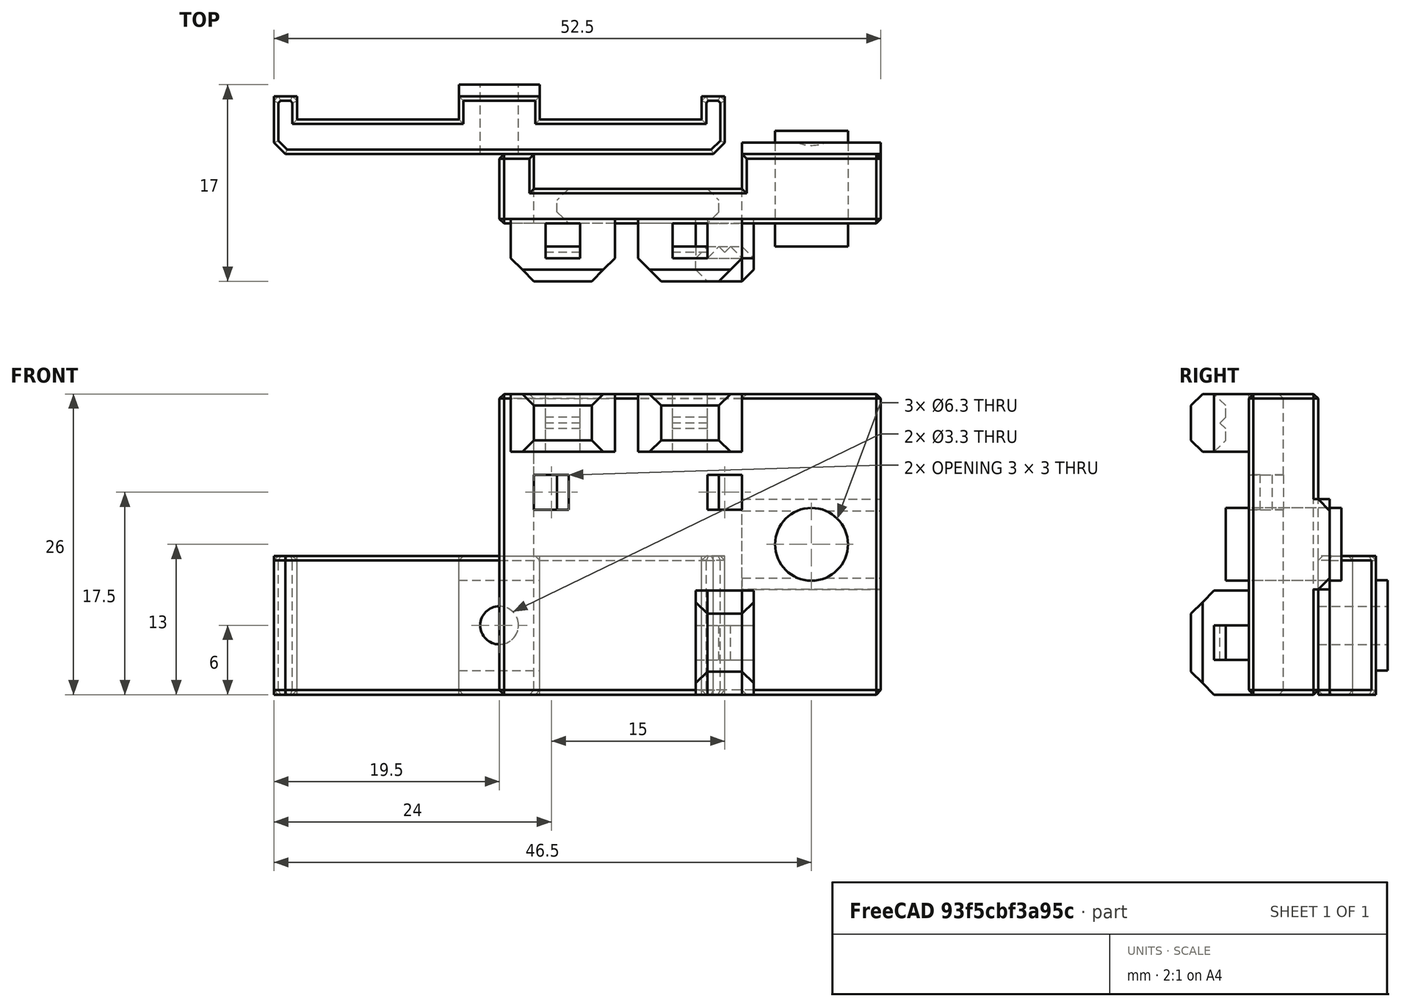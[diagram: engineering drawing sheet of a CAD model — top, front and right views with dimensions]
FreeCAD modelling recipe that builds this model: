
FCSTD DOCUMENT  (FreeCAD 0.19R24291 (Git))
Label: ribbon-cable-holder
License: Other
LicenseURL: GPL3
objects: Part::Box×21, Part::Chamfer×20, Part::Cut×10, Part::MultiFuse×10, Part::Feature×6, Part::Cylinder×5, Part::Refine×1
note: 73 computed .brp shape members not serialized (recipe doc carries the construction recipe); baked Part::Feature solids carry a one-line shape summary decoded from their .brp

FEATURE [Part::Feature] Body001
  shape: bbox 33 x 6 x 26 mm, 10 faces (baked)
FEATURE [Part::Chamfer] Chamfer
  Base = -> Body001
  Edges = 20 edges r=0.4: [Edge1,Edge3,Edge4,Edge6,Edge7,Edge9,Edge10,Edge12,Edge13,Edge14,Edge15,Edge16,Edge17,Edge18,Edge19,Edge20,Edge21,Edge22,Edge23,Edge24]
FEATURE [Part::Cylinder] Cylinder
  Angle = 360
  AttacherType = Attacher::AttachEngine3D
  Height = 10
  Placement = pos=(27,2,13) rot=(1,0,0;1.5708rad)
  Radius = 3.15
FEATURE [Part::Box] Box  label="Cube"
  AttacherType = Attacher::AttachEngine3D
  Height = 9
  Length = 3
  Placement = pos=(18,-11,0) rot=(0,0,1;0rad)
  Width = 6
FEATURE [Part::Box] Box001  label="Cube001"
  AttacherType = Attacher::AttachEngine3D
  Height = 3
  Length = 3
  Placement = pos=(18,-8,3) rot=(0,0,1;0rad)
  Width = 2
FEATURE [Part::Chamfer] Chamfer001
  Base = -> Box
  Edges = 2 edges r=2: [Edge9,Edge10]
FEATURE [Part::Cut] Cut
  Base = -> Chamfer001
  Tool = -> Box001
FEATURE [Part::Chamfer] Chamfer002
  Base = -> Cut
  Edges = 2 edges r=1: [Edge7,Edge24]
FEATURE [Part::Box] Box002  label="Cube002"
  AttacherType = Attacher::AttachEngine3D
  Height = 3
  Length = 2
  Placement = pos=(3,-7,18) rot=(0,0,1;0rad)
  Width = 6
FEATURE [Part::Box] Box003  label="Cube003"
  AttacherType = Attacher::AttachEngine3D
  Height = 3
  Length = 2
  Placement = pos=(19,-7,18) rot=(0,0,1;0rad)
  Width = 6
FEATURE [Part::MultiFuse] Fusion
  Placement = pos=(0,0,-2) rot=(0,0,1;0rad)
  Shapes = -> [Box003,Box002]
FEATURE [Part::Cylinder] Cylinder001
  Angle = 360
  AttacherType = Attacher::AttachEngine3D
  Height = 10
  Placement = pos=(27,2,13) rot=(1,0,0;1.5708rad)
  Radius = 3.15
FEATURE [Part::Cut] Cut001
  Base = -> Chamfer
  Tool = -> Fusion
FEATURE [Part::MultiFuse] Fusion001
  Shapes = -> [Cut001,Chamfer002]
FEATURE [Part::Box] Box004  label="Cube004"
  AttacherType = Attacher::AttachEngine3D
  Height = 7.8
  Length = 12
  Placement = pos=(21,-1,9.1) rot=(0,0,1;0rad)
  Width = 2
FEATURE [Part::Chamfer] Chamfer003
  Base = -> Box004
  Edges = 1 edges r=1: [Edge11]
FEATURE [Part::MultiFuse] Fusion002
  Shapes = -> [Fusion001,Chamfer003]
FEATURE [Part::Cut] Cut002
  Base = -> Fusion002
  Tool = -> Cylinder
FEATURE [Part::Chamfer] Chamfer004
  Base = -> Cut002
  Edges = 4 edges r=1: [Edge26,Edge31,Edge67,Edge80]
FEATURE [Part::Box] Box005  label="Cube005"
  AttacherType = Attacher::AttachEngine3D
  Height = 12
  Length = 7
  Placement = pos=(-3.5,0,0) rot=(0,0,1;0rad)
  Width = 5
FEATURE [Part::Box] Box006  label="Cube006"
  AttacherType = Attacher::AttachEngine3D
  Height = 12
  Length = 14
  Placement = pos=(3.5,0,0) rot=(0,0,1;0rad)
  Width = 3
FEATURE [Part::Box] Box007  label="Cube007"
  AttacherType = Attacher::AttachEngine3D
  Height = 12
  Length = 2
  Placement = pos=(17.5,0,0) rot=(0,0,1;0rad)
  Width = 5
FEATURE [Part::Box] Box008  label="Cube008"
  AttacherType = Attacher::AttachEngine3D
  Height = 12
  Length = 14
  Placement = pos=(-17.5,0,0) rot=(0,0,1;0rad)
  Width = 3
FEATURE [Part::Box] Box009  label="Cube009"
  AttacherType = Attacher::AttachEngine3D
  Height = 12
  Length = 2
  Placement = pos=(-19.5,0,0) rot=(0,0,1;0rad)
  Width = 5
FEATURE [Part::Box] Box010  label="Cube010"
  AttacherType = Attacher::AttachEngine3D
  Height = 7.8
  Length = 7
  Placement = pos=(-3.5,4,2.1) rot=(0,0,1;0rad)
  Width = 2
FEATURE [Part::Cylinder] Cylinder002
  Angle = 360
  AttacherType = Attacher::AttachEngine3D
  Height = 10
  Placement = pos=(0,1e-15,6) rot=(-1,0,0;1.5708rad)
  Radius = 1.65
FEATURE [Part::MultiFuse] Fusion003
  Shapes = -> [Box010,Box005,Box006,Box007,Box008,Box009]
FEATURE [Part::Cut] Cut003
  Base = -> Fusion003
  Tool = -> Cylinder002
FEATURE [Part::Refine] Cut003001
  Source = -> Cut003
FEATURE [Part::Chamfer] Chamfer005
  Base = -> Cut003001
  Edges = 2 edges r=1: [Edge11,Edge48]
FEATURE [Part::Chamfer] Chamfer006
  Base = -> Cut003001
  Edges = 2 edges r=1: [Edge11,Edge48]
FEATURE [Part::Chamfer] Chamfer007
  Base = -> Chamfer006
  Edges = 4 edges r=0.4: [Edge4,Edge21,Edge38,Edge44]
FEATURE [Part::Chamfer] Chamfer008
  Base = -> Chamfer007
  Edges = 36 edges r=0.4: [Edge1,Edge3,Edge5,Edge6,Edge7,Edge8,Edge9,Edge10,Edge11,Edge12,Edge13,Edge14,Edge15,Edge16,Edge17,Edge18,Edge19,Edge20,Edge21,Edge22,Edge24,Edge26,Edge27,Edge28,Edge29,Edge30,Edge31,Edge32,Edge33,Edge34,Edge35,Edge36,Edge37,Edge38,Edge39,Edge40]
FEATURE [Part::Box] Box011  label="Cube011"
  AttacherType = Attacher::AttachEngine3D
  Height = 9
  Length = 3
  Placement = pos=(18,-11,0) rot=(0,0,1;0rad)
  Width = 6
FEATURE [Part::Chamfer] Chamfer012
  Base = -> Box011
  Edges = 2 edges r=2: [Edge9,Edge10]
FEATURE [Part::Box] Box012  label="Cube012"
  AttacherType = Attacher::AttachEngine3D
  Height = 3
  Length = 2
  Placement = pos=(19,-7,18) rot=(0,0,1;0rad)
  Width = 6
FEATURE [Part::Box] Box013  label="Cube013"
  AttacherType = Attacher::AttachEngine3D
  Height = 7.8
  Length = 12
  Placement = pos=(21,-1,9.1) rot=(0,0,1;0rad)
  Width = 2
FEATURE [Part::Chamfer] Chamfer011
  Base = -> Box013
  Edges = 1 edges r=1: [Edge11]
FEATURE [Part::Box] Box014  label="Cube014"
  AttacherType = Attacher::AttachEngine3D
  Height = 3
  Length = 2
  Placement = pos=(3,-7,18) rot=(0,0,1;0rad)
  Width = 6
FEATURE [Part::MultiFuse] Fusion004
  Placement = pos=(0,0,-2) rot=(0,0,1;0rad)
  Shapes = -> [Box012,Box014]
FEATURE [Part::Box] Box015  label="Cube015"
  AttacherType = Attacher::AttachEngine3D
  Height = 3
  Length = 3
  Placement = pos=(18,-8,3) rot=(0,0,1;0rad)
  Width = 2
FEATURE [Part::Cylinder] Cylinder003
  Angle = 360
  AttacherType = Attacher::AttachEngine3D
  Height = 10
  Placement = pos=(27,2,13) rot=(1,0,0;1.5708rad)
  Radius = 3.15
FEATURE [Part::Cut] Cut003004
  Base = -> Chamfer012
  Tool = -> Box015
FEATURE [Part::Chamfer] Chamfer013
  Base = -> Cut003004
  Edges = 2 edges r=1: [Edge7,Edge24]
  Placement = pos=(-1,0,0) rot=(0,0,1;0rad)
FEATURE [Part::Feature] Body002
  shape: bbox 33 x 6 x 26 mm, 10 faces (baked)
FEATURE [Part::Chamfer] Chamfer010
  Base = -> Body002
  Edges = 20 edges r=0.4: [Edge1,Edge3,Edge4,Edge6,Edge7,Edge9,Edge10,Edge12,Edge13,Edge14,Edge15,Edge16,Edge17,Edge18,Edge19,Edge20,Edge21,Edge22,Edge23,Edge24]
FEATURE [Part::Cut] Cut003003
  Base = -> Chamfer010
  Tool = -> Fusion004
FEATURE [Part::Feature] Chamfer013001
  Placement = pos=(-1,0,0) rot=(0,0,1;0rad)
  shape: bbox 3 x 6 x 9 mm, 14 faces (baked)
FEATURE [Part::Feature] Chamfer013002
  Placement = pos=(1,0,0) rot=(0,0,1;0rad)
  shape: bbox 3 x 6 x 9 mm, 14 faces (baked)
FEATURE [Part::MultiFuse] Fusion006
  Shapes = -> [Chamfer013001,Chamfer013002]
FEATURE [Part::MultiFuse] Fusion007
  Shapes = -> [Fusion006,Cut003003,Chamfer011]
FEATURE [Part::Cut] Cut003005
  Base = -> Fusion007
  Tool = -> Cylinder003
FEATURE [Part::Chamfer] Chamfer013003
  Base = -> Cut003005
  Edges = 6 edges r=1: [Edge6,Edge32,Edge35,Edge71,Edge96,Edge102]
FEATURE [Part::Box] Box016  label="Cube016"
  AttacherType = Attacher::AttachEngine3D
  Height = 9
  Length = 3
  Placement = pos=(18,-11,0) rot=(0,0,1;0rad)
  Width = 6
FEATURE [Part::Chamfer] Chamfer013007
  Base = -> Box016
  Edges = 2 edges r=2: [Edge9,Edge10]
FEATURE [Part::Box] Box017  label="Cube017"
  AttacherType = Attacher::AttachEngine3D
  Height = 3
  Length = 2
  Placement = pos=(19,-7,18) rot=(0,0,1;0rad)
  Width = 6
FEATURE [Part::Box] Box018  label="Cube018"
  AttacherType = Attacher::AttachEngine3D
  Height = 7.8
  Length = 12
  Placement = pos=(21,-1,9.1) rot=(0,0,1;0rad)
  Width = 2
FEATURE [Part::Box] Box019  label="Cube019"
  AttacherType = Attacher::AttachEngine3D
  Height = 3
  Length = 2
  Placement = pos=(3,-7,18) rot=(0,0,1;0rad)
  Width = 6
FEATURE [Part::MultiFuse] Fusion008
  Placement = pos=(0,0,-2) rot=(0,0,1;0rad)
  Shapes = -> [Box017,Box019]
FEATURE [Part::Box] Box020  label="Cube020"
  AttacherType = Attacher::AttachEngine3D
  Height = 3
  Length = 3
  Placement = pos=(18,-8,3) rot=(0,0,1;0rad)
  Width = 2
FEATURE [Part::Cylinder] Cylinder004
  Angle = 360
  AttacherType = Attacher::AttachEngine3D
  Height = 10
  Placement = pos=(27,2,13) rot=(1,0,0;1.5708rad)
  Radius = 3.15
FEATURE [Part::Cut] Cut003008
  Base = -> Chamfer013007
  Tool = -> Box020
FEATURE [Part::Chamfer] Chamfer013008
  Base = -> Cut003008
  Edges = 2 edges r=1: [Edge7,Edge24]
  Placement = pos=(1,0,0) rot=(0,0,1;0rad)
FEATURE [Part::Feature] Body003
  shape: bbox 33 x 6 x 26 mm, 10 faces (baked)
FEATURE [Part::Chamfer] Chamfer013005
  Base = -> Body003
  Edges = 20 edges r=0.4: [Edge1,Edge3,Edge4,Edge6,Edge7,Edge9,Edge10,Edge12,Edge13,Edge14,Edge15,Edge16,Edge17,Edge18,Edge19,Edge20,Edge21,Edge22,Edge23,Edge24]
FEATURE [Part::Cut] Cut003007
  Base = -> Chamfer013005
  Tool = -> Fusion008
FEATURE [Part::MultiFuse] Fusion009
  Shapes = -> [Chamfer013,Chamfer013008]
FEATURE [Part::Chamfer] Chamfer013009
  Base = -> Fusion009
  Edges = 2 edges r=1: [Edge7,Edge70]
  Placement = pos=(10,0,4) rot=(0,1,0;4.71239rad)
FEATURE [Part::Feature] Chamfer013009001
  Placement = pos=(21,0,4) rot=(0,-1,0;1.5708rad)
  shape: bbox 9 x 6 x 5 mm, 37 faces (baked)
FEATURE [Part::Chamfer] Chamfer013009002
  Base = -> Box018
  Edges = 1 edges r=1: [Edge12]
FEATURE [Part::MultiFuse] Fusion010
  Shapes = -> [Chamfer013009002,Cut003007,Chamfer013009001,Chamfer013009]
FEATURE [Part::Cut] Cut003009
  Base = -> Fusion010
  Tool = -> Cylinder004
FEATURE [Part::Chamfer] Chamfer013009003
  Base = -> Cut003009
  Edges = 4 edges r=1: [Edge39,Edge44,Edge74,Edge88]
